# Revit family: Storage-Teknion-PCLS_Literatura-R2015
name_source: partatom
category: Furniture
revit_build: Autodesk Revit Architecture 2015 (Build: 20140323_1530(x64)
units: mm (PartAtom-declared; Revit-internal decimal feet)

## types (5) — shared parameters
Assembly Code = E2020200
Default Elevation = 48 "
Manufacturer = Teknion
Manufacturer Fax = 416.661.4586
Part Number = PCLS
Product Documentation Link = https://d2r72yk5wmppdj.cloudfront.net
Product Line = Punt Collection
Product Page URL = https://www.teknion.com
Series = Punt Collection
Sustainability Data = http://www.teknion.com
URL = www.teknion.com
Unit Weight URL = http://www.teknion.com
Warranty = http://www.teknion.com

## per-type parameters (varying)
| type | (BH) Bottom Hinged Door, 13" Height | (CS) Closed Storage, 28" Height | (DD) Double Drawers, 13" Height | (OD) Open Storage w Dividers, 13" Height | (OS) Open Storage, 13" Height | Closed Storage Drawer Cut Hole Depth | Description | Double Divider Hole Depth | End Gable Length Offset | Front Drawer Visibility | Height | Model |
| Bottom Hinged Door, 13" Height | Yes | No | No | No | No | 0.5 " | Literatura Storage, Bottom Hinged Door, 13" Height | 0.5 " | 0.984 " | Yes | 13.661 " | PCLSBH_ |
| Closed Storage, 28" Height | No | Yes | No | No | No | 1.537 " | Literatura Storage, Closed Storage, 28" Height, 35" Width | 0.5 " | 0.984 " | Yes | 27.933 " | PCLSCS35 |
| Open Storage w Dividers, 13" Height | No | No | No | Yes | No | 0.5 " | Literatura Storage, Open Storage w Dividers, 13" Height | 0.5 " | 0 " | No | 13.661 " | PCLSOD_ |
| Open Storage, 13" Height | No | No | No | No | Yes | 0.5 " | Literatura Storage, Open Storage, 13" Height | 0.5 " | 0 " | No | 13.661 " | PCLSOS_ |
| Double Drawers, 13" Height | No | No | Yes | No | No | 0.5 " | Literatura Storage, Double Drawers, 13" Height, 35" Width | 1.537 " | 0.984 " | Yes | 13.661 " | PCLSDD35 |

## geometry (parser evidence)
native form markers: Sweep x2
no freeform markers — native parametric forms only
